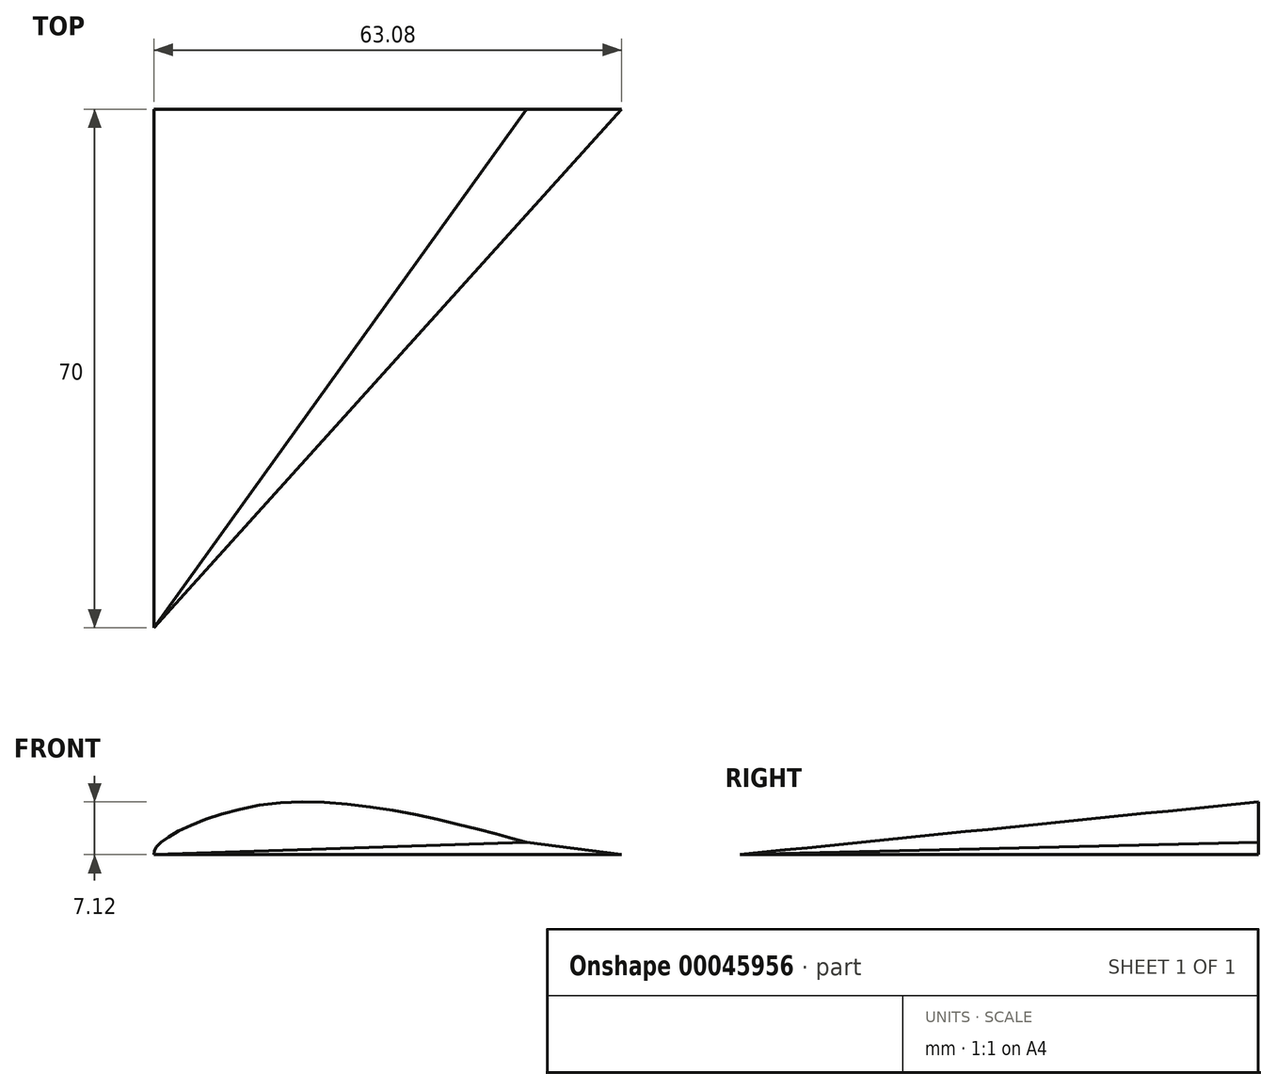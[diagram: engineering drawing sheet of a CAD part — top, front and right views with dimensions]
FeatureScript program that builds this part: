
annotation { "Feature Type Name" : "Feature", "Feature Type Description" : "" }
export const myFeature = defineFeature(function(context is Context, id is Id, definition is map)
    precondition{}
    {
        {
            var Q0;
            Q0=qCreatedBy(makeId("Front.planeOp"),FACE);
            var sketch = newSketch(context, id + "F0", { "sketchPlane" : qUnion([Q0])});
            skFitSpline(sketch, "E0", {"points": [v(16.77, 0) * mm, v(3.98, 1.65) * mm, v(-28.88, 7.02) * mm, v(-45.74, 1.3) * mm, v(-46.31, 0) * mm], "startDerivative": vector(-83.03, 2.65) * mm, "endDerivative": vector(0.3, -16.25) * mm});
            skLineSegment(sketch, "E1", {"start": v(-46.31, 0) * mm, "end": v(16.77, 0) * mm});
            skLineSegment(sketch, "E2", {"start": v(3.98, 1.65) * mm, "end": v(3.98, 0) * mm});
            skSolve(sketch);
        }
        {
            var Q0;
            Q0=qCreatedBy(makeId("Top.planeOp"),FACE);
            var sketch = newSketch(context, id + "F1", { "sketchPlane" : qUnion([Q0])});
            skLineSegment(sketch, "E3", {"start": v(-46.31, -70) * mm, "end": v(-4.23, -70) * mm});
            skLineSegment(sketch, "E4", {"start": v(-46.31, -70) * mm, "end": v(-46.31, 0) * mm});
            skSolve(sketch);
        }
        {
            var Q0;
            {var subQ0=sQuery(id+"F0.wireOp",EDGE,"E2");Q0=makeQuery(id+"F0.imprint","IMPRINT",FACE,{"disambiguationData":[TD([[makeQuery(id+"F0.imprint","IMPRINT",EDGE,{"derivedFrom":subQ0}),-1.0]])]});}
            var Q1;
            Q1=sQuery(id+"F1.wireOp",VERTEX,"E3.start");
            loft(context, id + "F2", {"sheetProfilesArray" : [{ "sheetProfileEntities" : qUnion([Q0]) }, { "sheetProfileEntities" : qUnion([Q1]) }]});
        }
        {
            var Q1;
            {var subQ0=sQuery(id+"F0.wireOp",EDGE,"E0");var subQ1=sQuery(id+"F0.wireOp",EDGE,"E1");var subQ2=sQuery(id+"F0.wireOp",EDGE,"E2");Q1=makeQuery(id+"F2.opLoft","SWEPT_FACE",FACE,{"disambiguationData":[OSD([subQ0,subQ1,subQ2]),TDD([makeQuery(id+"F0.imprint","INTERSECT",VERTEX,{"derivedFrom":[subQ0,subQ2]}),makeQuery(id+"F0.imprint","INTERSECT",VERTEX,{"derivedFrom":[subQ1,subQ2]}),makeQuery(id+"F0.imprint","IMPRINT",EDGE,{"derivedFrom":subQ2})])]});}
            var Q2;
            Q2=sQuery(id+"F0.wireOp",VERTEX,"E0.start");
            loft(context, id + "F3", {"operationType" : NewBodyOperationType.ADD, "sheetProfilesArray" : [{ "sheetProfileEntities" : qUnion([Q1]) }, { "sheetProfileEntities" : qUnion([Q2]) }]});
        }
    });
